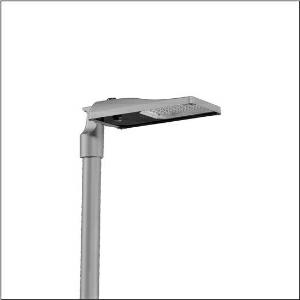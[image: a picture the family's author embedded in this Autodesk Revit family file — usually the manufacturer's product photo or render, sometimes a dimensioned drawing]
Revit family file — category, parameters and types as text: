
# Revit family: streetlight_sl_31_mini___st1_0a_5xh2d71t08ha_58cf
name_source: partatom
category: Lighting Fixtures
units: mm (PartAtom-declared; Revit-internal decimal feet)

## family parameters
Cut with Voids When Loaded = No
Host = Face
Light Source = No
Part Type = Normal
Room Calculation Point = No
Round Connector Dimension = Use Diameter
Shared = No

## types (1)
- --- (1 x LED, 7620 lm, 68.3 W, 2200K)
    Apparent Load = 68 VA
    CIE Flux Codes = 37 72 97 100 100
    Color Rendering = 70
    Color Temperature = 2200K
    Default Elevation = 1800 mm
    Description = Streetlight SL 31 mini D4i, Desk-Remote mast luminaire for post-top, side-entry; light control with lens of PMMA; light distribution: ST1.0a, direct asymmetric distribution, for standard-compliant lighting for roads and squares; LED: luminous flux: 7.620lm, light colour: 722, colour temperature: 2200K; luminous efficacy: 111,6lm/W; control: pre-setting: logarithmic dimming characteristic, flexible luminous flux parameterisation, time-dependent luminous flux control, constant luminous flux control, power reduction, intelligent temperature release in ECG and LED module, overheat protection; luminaire housing, of diecast aluminium, Siteco® metallic grey (DB 702S), corrosivity category C5 high according to DIN EN ISO 12944; cover of toughened safety glass, transparent, mast flange of diecast aluminium, Siteco® metallic grey (DB 702S), spigot size: 76/60mm, mast flange included unmounted; with cable H07RN-F 2x 1.5mm², cable length: 8,5m, connection cable pre-assembled; mains connection: 220..240V, AC, 50/60Hz; power consumption (at start of service life): 68,3W / (at end of service life): 74,5W / (with reduced operation 50%): 29,2W; protection rating (complete): IP66; insulation class (complete): insulation class II (safety insulation); impact resistance: IK09; certification: CE, ENEC, ENEC+, VDE, UKCA, ZD4i; permissible operating ambient temperature for outdoor applications: -40..+50°C; packaging unit: 1 piece

Light Distribution: ST1.0a
    Height = 76 mm
    Lamp = 1 x LED
    Lamp Light Flux = 7620 lm
    Lamp Power = 68.3 W
    Lamp count = 1
    Length = 547 mm
    Luminous efficacy = 112 lm/W
    Manufacturer = Siteco
    ModVariant = No
    Model = 5XH2D71T08HA
    Number of Poles = 1
    OnlyDefault = Yes
    Power Factor = 1
    Product Name = Streetlight SL 31 mini | ST1.0a
    Product group = mast luminaire | pylon top
    ProductGroupID = 6100
    Protection Class = Protection class II
    Protection Degree = IP 66
    RLX_Detail_Level = 1
    RLX_Emergency_Light_Flux = 0 lm
    RLX_Emergency_Type = 0
    RLX_Emergency_Type_DB = No
    RlxData = <blob elided: 24253 chars, md5=0bf77c20>
    Socket = socket
    Standby Power = 0 W
    System Light Flux = 7620 lm
    System Power = 68 W
    Type Comments = factory setting: luminous flux: 100 % | dim-lin: 254 | 692 mA
    Type Image = l_1300332.jpg
    URL = http://relux.com
    VarID = @adj_002211
    Voltage = 0 V
    Weight = 0.00 kg
    Width = 265 mm

## geometry (parser evidence)
native form markers: Blend x4, Sweep x11
no freeform markers — native parametric forms only
